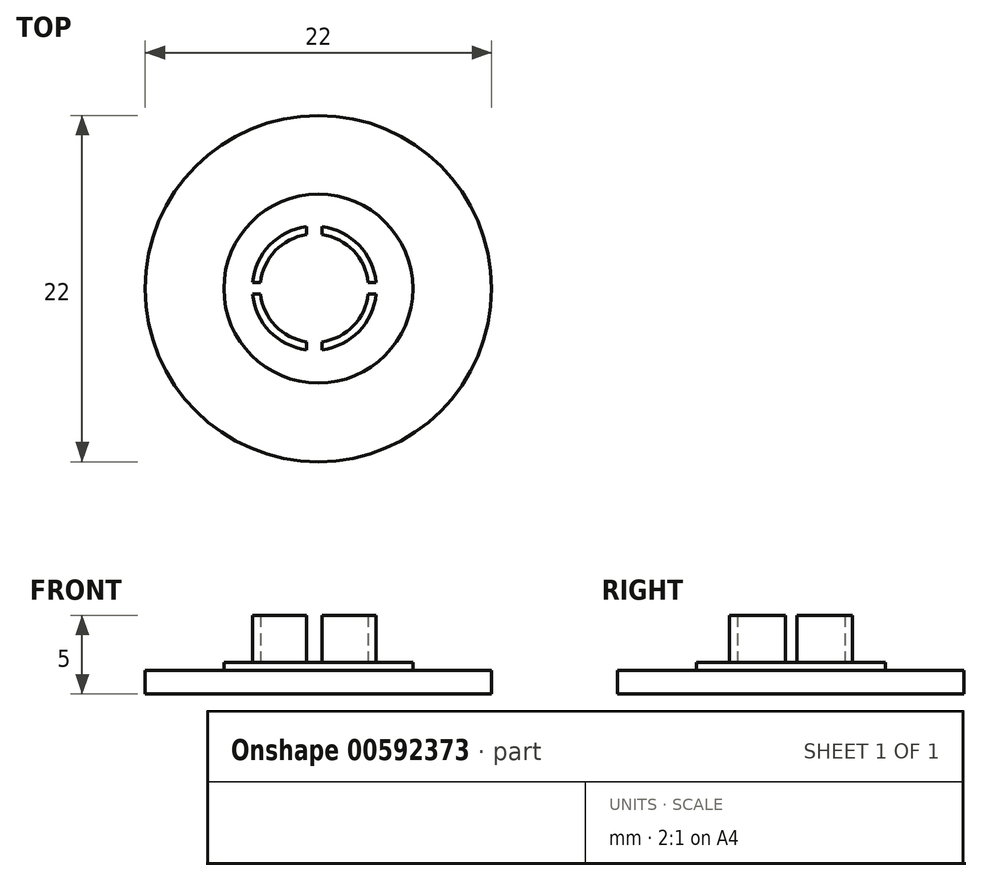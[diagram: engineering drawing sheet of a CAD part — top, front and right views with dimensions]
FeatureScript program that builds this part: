
annotation { "Feature Type Name" : "Feature", "Feature Type Description" : "" }
export const myFeature = defineFeature(function(context is Context, id is Id, definition is map)
    precondition{}
    {
        {
            var Q0;
            Q0=qCreatedBy(makeId("Top.planeOp"),FACE);
            var sketch = newSketch(context, id + "F0", { "sketchPlane" : qUnion([Q0])});
            skCircle(sketch, "E0", {"center": v(0, 0) * mm, "radius": 11.15 * mm});
            skLineSegment(sketch, "E1", {"start": v(0, 0) * mm, "end": v(0, 24.65) * mm});
            skCircle(sketch, "E2", {"center": v(0, 24.65) * mm, "radius": 10.8 * mm});
            skCircle(sketch, "E3.1.0", {"center": v(-21.35, -12.32) * mm, "radius": 10.8 * mm});
            skCircle(sketch, "E3.2.0", {"center": v(21.35, -12.32) * mm, "radius": 10.8 * mm});
            skArc(sketch, "E4.0", {"start": v(11.2, 17.1) * mm, "mid": v(0, 38.15) * mm, "end": v(-11.2, 17.1) * mm});
            skArc(sketch, "E5.0", {"start": v(-1.28, -13.8) * mm, "mid": v(0, -13.85) * mm, "end": v(1.28, -13.8) * mm});
            skArc(sketch, "E6.0", {"start": v(9.22, -18.25) * mm, "mid": v(33.04, -19.08) * mm, "end": v(20.4, 1.14) * mm});
            skArc(sketch, "E7.0", {"start": v(-20.4, 1.14) * mm, "mid": v(-33.04, -19.07) * mm, "end": v(-9.22, -18.25) * mm});
            skArc(sketch, "E8.trimOffspring", {"start": v(12.58, 5.78) * mm, "mid": v(12, 6.92) * mm, "end": v(11.3, 8) * mm});
            skArc(sketch, "E9.trimOffspring", {"start": v(-11.3, 8) * mm, "mid": v(-12, 6.92) * mm, "end": v(-12.58, 5.78) * mm});
            skArc(sketch, "E10.filletArc", {"start": v(-11.3, 8) * mm, "mid": v(-9.83, 12.54) * mm, "end": v(-11.2, 17.1) * mm});
            skArc(sketch, "E11.filletArc", {"start": v(-20.4, 1.14) * mm, "mid": v(-15.77, 2.24) * mm, "end": v(-12.58, 5.78) * mm});
            skArc(sketch, "E12.filletArc", {"start": v(-1.28, -13.8) * mm, "mid": v(-5.95, -14.78) * mm, "end": v(-9.22, -18.25) * mm});
            skArc(sketch, "E13.filletArc", {"start": v(9.22, -18.25) * mm, "mid": v(5.95, -14.78) * mm, "end": v(1.28, -13.8) * mm});
            skArc(sketch, "E14.filletArc", {"start": v(12.58, 5.78) * mm, "mid": v(15.77, 2.24) * mm, "end": v(20.4, 1.14) * mm});
            skArc(sketch, "E15.filletArc", {"start": v(11.2, 17.1) * mm, "mid": v(9.83, 12.54) * mm, "end": v(11.3, 8) * mm});
            skSolve(sketch);
        }
        {
            var Q0;
            Q0=qCreatedBy(makeId("Top.planeOp"),FACE);
            var sketch = newSketch(context, id + "F1", { "sketchPlane" : qUnion([Q0])});
            skCircle(sketch, "E16", {"center": v(-26.13, 14.36) * mm, "radius": 11 * mm});
            skSolve(sketch);
        }
        {
            var Q0;
            Q0 = qSketchRegion(id + "F1", true);
            extrude(context, id + "F2", {"entities" : qUnion([Q0]), "depth" : 1.5 * mm, "offsetDistance" : 25 * mm});
        }
        {
            var Q0;
            Q0=makeQuery(id+"F2.opExtrude","CAP_FACE",FACE,{"disambiguationData":[OSD([sQuery(id+"F1.wireOp",EDGE,"E16")])],"isStart":false});
            var sketch = newSketch(context, id + "F3", { "sketchPlane" : qUnion([Q0])});
            skSolve(sketch);
        }
        {
            var Q0;
            Q0=makeQuery(id+"F3.imprint","IMPRINT",FACE,{"disambiguationData":[TD([[makeQuery(id+"F3.imprint","IMPRINT",EDGE,{"derivedFrom":makeQuery(id+"F2.opExtrude","CAP_EDGE",EDGE,{"disambiguationData":[OSD([sQuery(id+"F1.wireOp",EDGE,"E16")])],"isStart":false})}),1.0]])]});
            var sketch = newSketch(context, id + "F4", { "sketchPlane" : qUnion([Q0])});
            skCircle(sketch, "E17.0", {"center": v(-26.13, 14.36) * mm, "radius": 6 * mm});
            skSolve(sketch);
        }
        {
            var Q0;
            Q0 = qSketchRegion(id + "F4", true);
            extrude(context, id + "F5", {"entities" : qUnion([Q0]), "operationType" : NewBodyOperationType.ADD, "depth" : .5 * mm, "offsetDistance" : 25 * mm});
        }
        {
            var Q0;
            Q0=makeQuery(id+"F5.opExtrude","CAP_FACE",FACE,{"disambiguationData":[OSD([sQuery(id+"F4.wireOp",EDGE,"E17.0")])],"isStart":false});
            var sketch = newSketch(context, id + "F6", { "sketchPlane" : qUnion([Q0])});
            skArc(sketch, "E18", {"start": v(-25.89, 10.48) * mm, "mid": v(-23.55, 11.65) * mm, "end": v(-22.46, 14.02) * mm});
            skArc(sketch, "E19", {"start": v(-25.89, 10.98) * mm, "mid": v(-23.9, 12) * mm, "end": v(-22.97, 14.02) * mm});
            skArc(sketch, "E20.trimOffspring", {"start": v(-29.8, 14.02) * mm, "mid": v(-28.87, 12) * mm, "end": v(-26.89, 10.98) * mm});
            skArc(sketch, "E21.trimOffspring", {"start": v(-30.31, 14.02) * mm, "mid": v(-29.22, 11.65) * mm, "end": v(-26.89, 10.48) * mm});
            skArc(sketch, "E22.trimOffspring", {"start": v(-26.89, 17.79) * mm, "mid": v(-28.87, 16.77) * mm, "end": v(-29.8, 14.75) * mm});
            skArc(sketch, "E23.trimOffspring", {"start": v(-26.89, 18.3) * mm, "mid": v(-29.22, 17.12) * mm, "end": v(-30.31, 14.75) * mm});
            skArc(sketch, "E24.trimOffspring", {"start": v(-22.46, 14.75) * mm, "mid": v(-23.55, 17.12) * mm, "end": v(-25.89, 18.3) * mm});
            skArc(sketch, "E25.trimOffspring", {"start": v(-22.97, 14.75) * mm, "mid": v(-23.9, 16.77) * mm, "end": v(-25.89, 17.79) * mm});
            skLineSegment(sketch, "E26", {"start": v(-25.89, 10.48) * mm, "end": v(-25.89, 10.98) * mm});
            skLineSegment(sketch, "E27", {"start": v(-26.89, 10.98) * mm, "end": v(-26.89, 10.48) * mm});
            skLineSegment(sketch, "E28", {"start": v(-29.8, 14.02) * mm, "end": v(-30.31, 14.02) * mm});
            skLineSegment(sketch, "E29", {"start": v(-30.31, 14.75) * mm, "end": v(-29.8, 14.75) * mm});
            skLineSegment(sketch, "E30", {"start": v(-26.89, 17.79) * mm, "end": v(-26.89, 18.3) * mm});
            skLineSegment(sketch, "E31", {"start": v(-25.89, 18.3) * mm, "end": v(-25.89, 17.79) * mm});
            skLineSegment(sketch, "E32", {"start": v(-22.97, 14.75) * mm, "end": v(-22.46, 14.75) * mm});
            skLineSegment(sketch, "E33", {"start": v(-22.46, 14.02) * mm, "end": v(-22.97, 14.02) * mm});
            skSolve(sketch);
        }
        {
            var Q0;
            Q0 = qSketchRegion(id + "F6", true);
            extrude(context, id + "F7", {"entities" : qUnion([Q0]), "operationType" : NewBodyOperationType.ADD, "depth" : 3 * mm, "offsetDistance" : 25 * mm});
        }
    });
